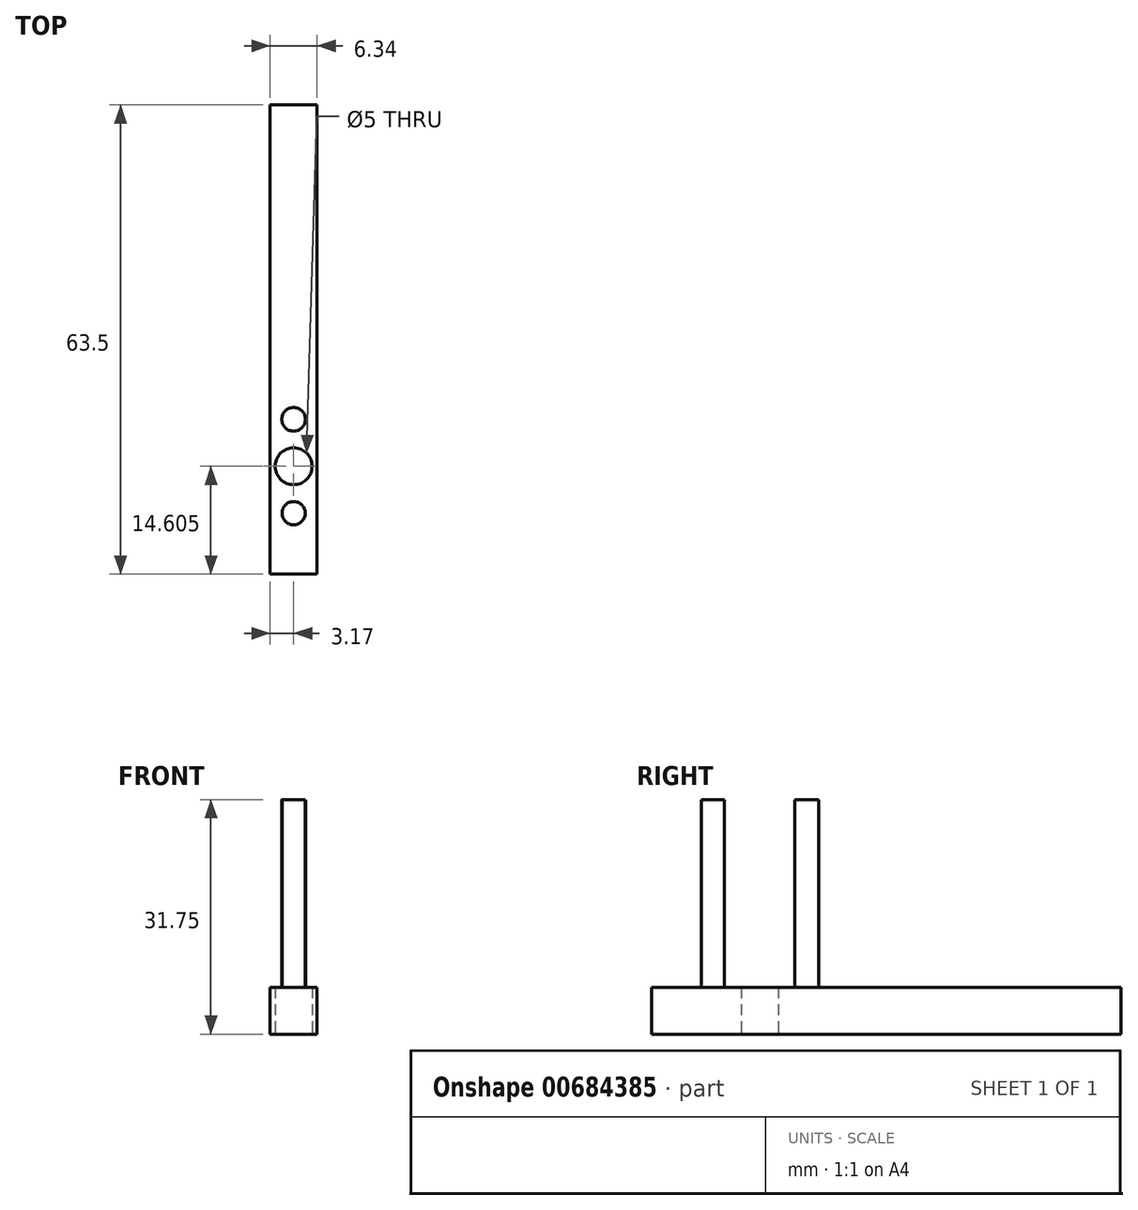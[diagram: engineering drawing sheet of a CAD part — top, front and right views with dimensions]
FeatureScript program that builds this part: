
annotation { "Feature Type Name" : "Feature", "Feature Type Description" : "" }
export const myFeature = defineFeature(function(context is Context, id is Id, definition is map)
    precondition{}
    {
        {
            var Q0;
            Q0=qCreatedBy(makeId("Top.planeOp"),FACE);
            var sketch = newSketch(context, id + "F0", { "sketchPlane" : qUnion([Q0])});
            skLineSegment(sketch, "E0.bottom", {"start": v(-3.17, 31.75) * mm, "end": v(3.18, 31.75) * mm});
            skLineSegment(sketch, "E0.top", {"start": v(-3.18, -31.75) * mm, "end": v(3.17, -31.75) * mm});
            skLineSegment(sketch, "E0.left", {"start": v(-3.17, 31.75) * mm, "end": v(-3.18, -31.75) * mm});
            skLineSegment(sketch, "E0.right", {"start": v(3.18, 31.75) * mm, "end": v(3.17, -31.75) * mm});
            skPoint(sketch, "E0.middle", {"position": v(0, 0) * mm});
            skCircle(sketch, "E1", {"center": v(0, -17.15) * mm, "radius": 2.5 * mm});
            skCircle(sketch, "E2", {"center": v(0, -10.8) * mm, "radius": 1.59 * mm, "construction": true});
            skCircle(sketch, "E3", {"center": v(0, -23.5) * mm, "radius": 1.59 * mm, "construction": true});
            skSolve(sketch);
        }
        {
            var Q0;
            Q0=makeQuery(id+"F0.imprint","IMPRINT",FACE,{"disambiguationData":[TD([[makeQuery(id+"F0.imprint","IMPRINT",EDGE,{"derivedFrom":sQuery(id+"F0.wireOp",EDGE,"E0.bottom")}),-1.0]])]});
            extrude(context, id + "F1", {"entities" : qUnion([Q0]), "depth" : 6.35 * mm, "offsetDistance" : 25.4 * mm});
        }
        {
            var Q0;
            Q0=makeQuery(id+"F1.opExtrude","CAP_FACE",FACE,{"disambiguationData":[OSD([sQuery(id+"F0.wireOp",EDGE,"E0.bottom"),sQuery(id+"F0.wireOp",EDGE,"E0.top"),sQuery(id+"F0.wireOp",EDGE,"E0.left"),sQuery(id+"F0.wireOp",EDGE,"E0.right"),sQuery(id+"F0.wireOp",EDGE,"E1")])],"isStart":false});
            var sketch = newSketch(context, id + "F2", { "sketchPlane" : qUnion([Q0])});
            skCircle(sketch, "E4", {"center": v(0, -10.8) * mm, "radius": 1.6 * mm});
            skCircle(sketch, "E5", {"center": v(0, -23.5) * mm, "radius": 1.57 * mm});
            skSolve(sketch);
        }
        {
            var Q0;
            Q0=makeQuery(id+"F2.imprint","IMPRINT",FACE,{"disambiguationData":[TD([[makeQuery(id+"F2.imprint","IMPRINT",EDGE,{"derivedFrom":sQuery(id+"F2.wireOp",EDGE,"E4")}),1.0]])]});
            var Q1;
            Q1=makeQuery(id+"F2.imprint","IMPRINT",FACE,{"disambiguationData":[TD([[makeQuery(id+"F2.imprint","IMPRINT",EDGE,{"derivedFrom":sQuery(id+"F2.wireOp",EDGE,"E5")}),1.0]])]});
            extrude(context, id + "F3", {"entities" : qUnion([Q0, Q1]), "operationType" : NewBodyOperationType.ADD, "depth" : 25.4 * mm, "offsetDistance" : 25.4 * mm});
        }
    });
